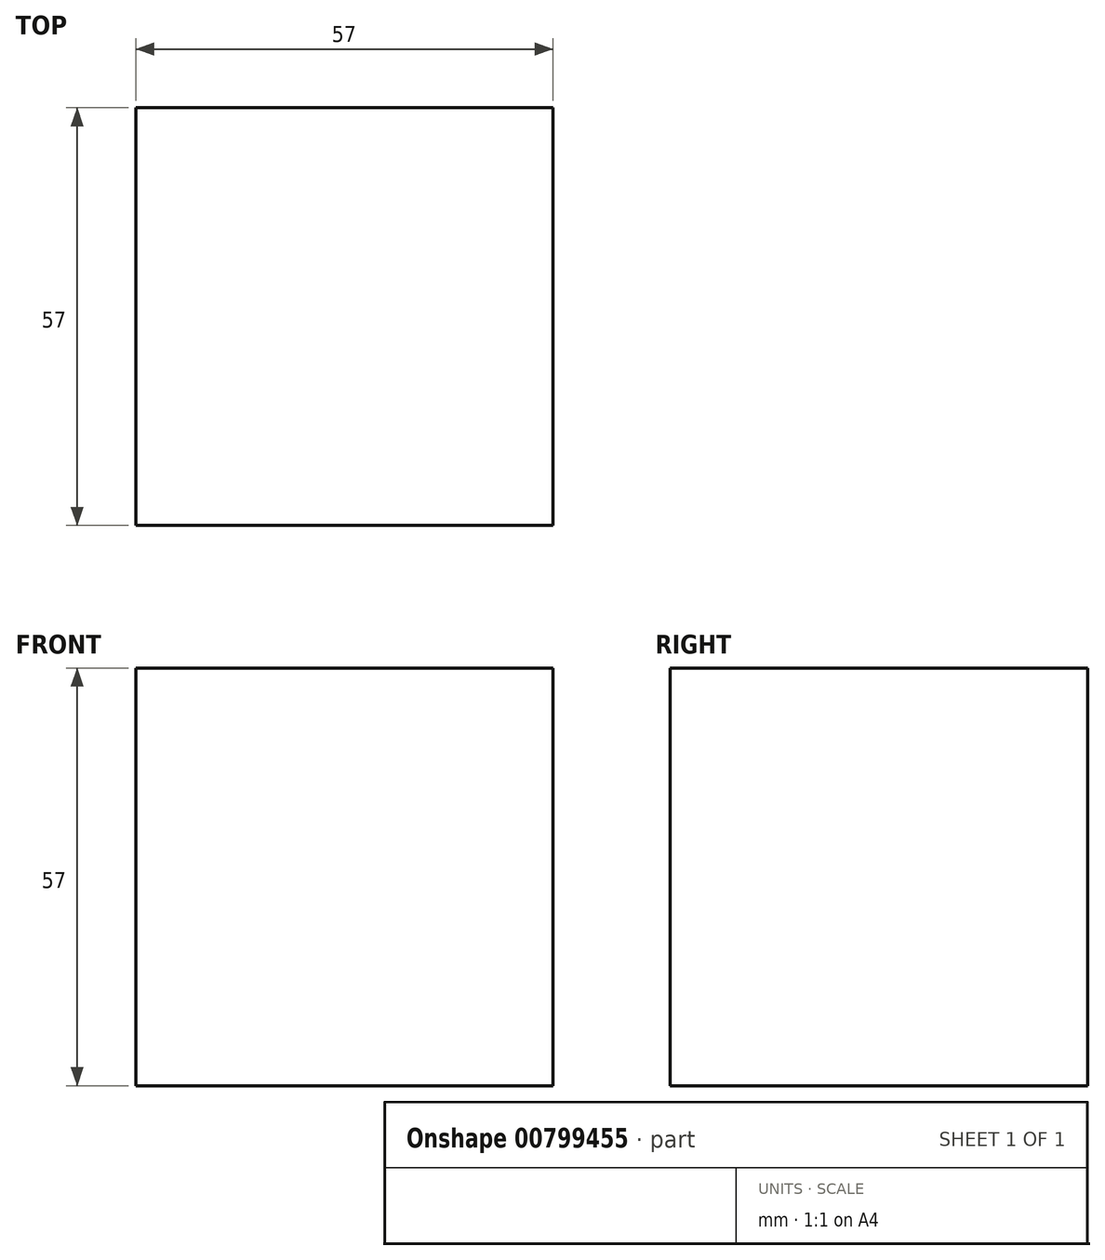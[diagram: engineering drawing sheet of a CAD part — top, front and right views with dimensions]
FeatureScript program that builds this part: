
annotation { "Feature Type Name" : "Feature", "Feature Type Description" : "" }
export const myFeature = defineFeature(function(context is Context, id is Id, definition is map)
    precondition{}
    {
        {
            var Q0;
            Q0=qCreatedBy(makeId("Top.planeOp"),FACE);
            var sketch = newSketch(context, id + "F0", { "sketchPlane" : qUnion([Q0])});
            skLineSegment(sketch, "E0.bottom", {"start": v(-28.5, 28.5) * mm, "end": v(28.5, 28.5) * mm});
            skLineSegment(sketch, "E0.top", {"start": v(-28.5, -28.5) * mm, "end": v(28.5, -28.5) * mm});
            skLineSegment(sketch, "E0.left", {"start": v(-28.5, 28.5) * mm, "end": v(-28.5, -28.5) * mm});
            skLineSegment(sketch, "E0.right", {"start": v(28.5, 28.5) * mm, "end": v(28.5, -28.5) * mm});
            skSolve(sketch);
        }
        {
            var Q0;
            Q0=makeQuery(id+"F0.imprint","IMPRINT",FACE,{"disambiguationData":[TD([[makeQuery(id+"F0.imprint","IMPRINT",EDGE,{"derivedFrom":sQuery(id+"F0.wireOp",EDGE,"E0.bottom")}),-1.0]])]});
            extrude(context, id + "F1", {"entities" : qUnion([Q0]), "depth" : 57 * mm, "offsetDistance" : 25 * mm});
        }
    });
